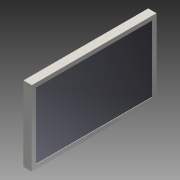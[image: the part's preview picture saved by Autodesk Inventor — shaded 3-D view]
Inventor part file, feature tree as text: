
AUTODESK INVENTOR PART (.ipt)
format: ipt  version: 2015 SP1 (Build 190203100, 203)  size: 97,792 bytes
history: native  units: in
note: dims shown in document units (in); Inventor stores cm internally (conversion verified against a paired STEP export)
features: extrude x2, sketch x2
ambient origin geometry x8: Origin, YZ Plane, XZ Plane, XY Plane, X Axis, Y Axis, Z Axis, Center Point
bodies: Solid1 (feature_tree)
feature tree (4):
  extrude  "Extrusion1"  Depth=18.0in
  extrude  "Extrusion2"  Depth=1.0in
  sketch  "Sketch1"  dims[d0=30.0in d1=18.0in]
  sketch  "Sketch2"  dims[d2=2.0in d3=0.0in d4=1.0in d5=0.1in d6=0.0in]
